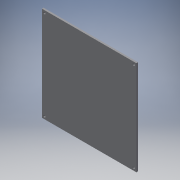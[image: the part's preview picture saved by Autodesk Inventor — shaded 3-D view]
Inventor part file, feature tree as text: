
AUTODESK INVENTOR PART (.ipt)
format: ipt  version: 2018 (Build 220112000, 112)  size: 111,616 bytes
history: native  units: in
note: dims shown in document units (in); Inventor stores cm internally (conversion verified against a paired STEP export)
features: extrude x2, sketch x2, chamfer x1, projected_geometry x1
ambient origin geometry x8: Origin, YZ Plane, XZ Plane, XY Plane, X Axis, Y Axis, Z Axis, Center Point
bodies: Solid1 (feature_tree)
feature tree (6):
  extrude  "Extrusion1"  Depth=8.6614in
  extrude  "Extrusion2"  Depth=0.0787in
  chamfer  "Chamfer1"  Distance=0.2362in
  sketch  "Sketch1"  dims[d0=8.6614in d1=8.6614in]
  sketch  "Sketch2"  dims[d2=0.1575in d3=0.0in d4=0.2362in d5=0.2362in d6=0.1181in d7=1.5748in d9=360.0deg d11=0.1575in d12=0.0in d13=0.0394in d14=0.0787in d15=45.0deg]
  projected_geometry  "Projected Loop1"
